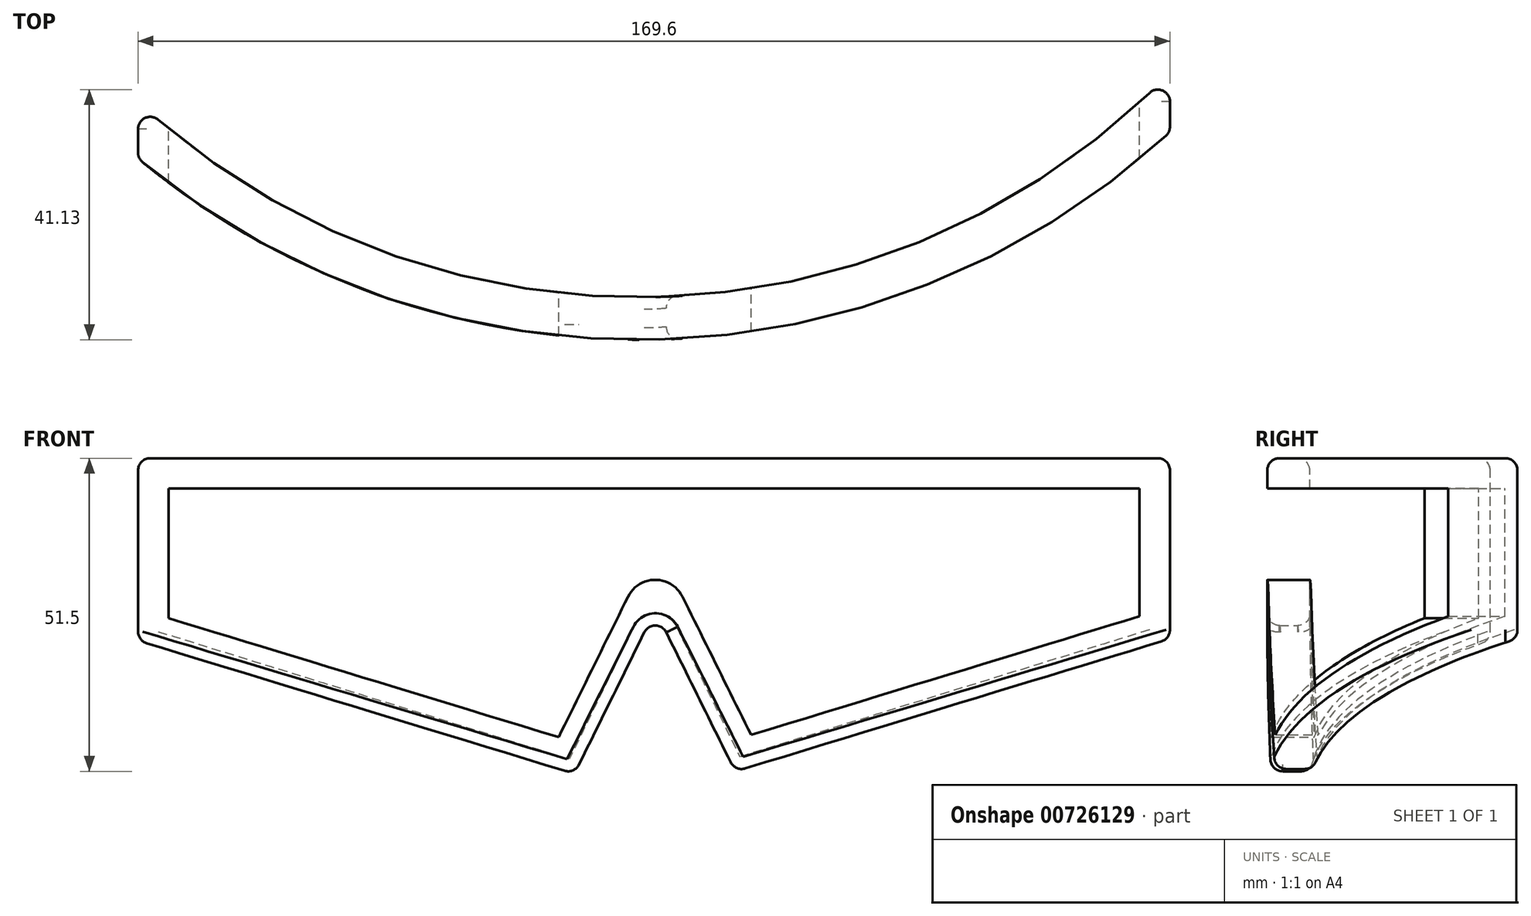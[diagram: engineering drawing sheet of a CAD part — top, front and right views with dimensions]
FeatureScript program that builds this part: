
annotation { "Feature Type Name" : "Feature", "Feature Type Description" : "" }
export const myFeature = defineFeature(function(context is Context, id is Id, definition is map)
    precondition{}
    {
        {
            var Q0;
            Q0=qCreatedBy(makeId("Front.planeOp"),FACE);
            var sketch = newSketch(context, id + "F0", { "sketchPlane" : qUnion([Q0])});
            skLineSegment(sketch, "E0.top", {"start": v(-14.32, 57.35) * mm, "end": v(-99.32, 57.35) * mm});
            skLineSegment(sketch, "E0.right", {"start": v(-99.32, 27.35) * mm, "end": v(-99.32, 57.35) * mm});
            skLineSegment(sketch, "E1", {"start": v(-27.59, 5.44) * mm, "end": v(-14.32, 32.35) * mm});
            skLineSegment(sketch, "E2", {"start": v(-27.59, 5.44) * mm, "end": v(-99.32, 27.35) * mm});
            skLineSegment(sketch, "E3.MirrorCS", {"start": v(-1.16, 5.82) * mm, "end": v(70.28, 27.64) * mm});
            skLineSegment(sketch, "E4.MirrorCS", {"start": v(70.28, 27.64) * mm, "end": v(70.28, 57.35) * mm});
            skLineSegment(sketch, "E5.MirrorCS", {"start": v(-14.32, 57.35) * mm, "end": v(70.28, 57.35) * mm});
            skLineSegment(sketch, "E6.MirrorCS", {"start": v(-1.16, 5.82) * mm, "end": v(-14.32, 32.35) * mm});
            skSolve(sketch);
        }
        {
            var Q0;
            Q0 = qSketchRegion(id + "F0", true);
            extrude(context, id + "F1", {"entities" : qUnion([Q0]), "depth" : 150 * mm, "offsetDistance" : 25 * mm});
        }
        {
            var Q0;
            Q0=qCreatedBy(makeId("Front.planeOp"),FACE);
            var sketch = newSketch(context, id + "F2", { "sketchPlane" : qUnion([Q0])});
            skLineSegment(sketch, "E7.0", {"start": v(65.28, 31.34) * mm, "end": v(1.43, 11.84) * mm});
            skLineSegment(sketch, "E7.1", {"start": v(65.28, 52.35) * mm, "end": v(65.28, 31.34) * mm});
            skLineSegment(sketch, "E7.2", {"start": v(-14.33, 43.62) * mm, "end": v(-30.2, 11.46) * mm});
            skLineSegment(sketch, "E7.3", {"start": v(-30.2, 11.46) * mm, "end": v(-94.32, 31.05) * mm});
            skLineSegment(sketch, "E7.4", {"start": v(-94.32, 31.05) * mm, "end": v(-94.32, 52.35) * mm});
            skLineSegment(sketch, "E7.5", {"start": v(1.43, 11.84) * mm, "end": v(-14.33, 43.62) * mm});
            skLineSegment(sketch, "E7.6", {"start": v(-94.32, 52.35) * mm, "end": v(65.28, 52.35) * mm});
            skSolve(sketch);
        }
        {
            var Q0;
            Q0 = qSketchRegion(id + "F2", true);
            extrude(context, id + "F3", {"entities" : qUnion([Q0]), "operationType" : NewBodyOperationType.REMOVE, "depth" : 200 * mm, "offsetDistance" : 25 * mm});
        }
        {
            var Q0;
            Q0=makeQuery(id+"F1.opExtrude","SWEPT_FACE",FACE,{"disambiguationData":[OSD([sQuery(id+"F0.wireOp",EDGE,"E0.top"),sQuery(id+"F0.wireOp",EDGE,"E5.MirrorCS")])]});
            var sketch = newSketch(context, id + "F4", { "sketchPlane" : qUnion([Q0])});
            skArc(sketch, "E8", {"start": v(-139.84, -48.26) * mm, "mid": v(-17.33, -138.81) * mm, "end": v(105.65, -48.9) * mm});
            skArc(sketch, "E9.0", {"start": v(-133.16, -46.2) * mm, "mid": v(-17.31, -131.81) * mm, "end": v(98.98, -46.8) * mm});
            skLineSegment(sketch, "E10", {"start": v(-139.84, -48.26) * mm, "end": v(-133.16, -46.2) * mm});
            skLineSegment(sketch, "E11", {"start": v(98.98, -46.8) * mm, "end": v(105.65, -48.9) * mm});
            skSolve(sketch);
        }
        {
            var Q0;
            Q0 = qSketchRegion(id + "F4", true);
            extrude(context, id + "F5", {"entities" : qUnion([Q0]), "operationType" : NewBodyOperationType.INTERSECT, "oppositeDirection" : true, "depth" : 150 * mm, "offsetDistance" : 25 * mm});
        }
        {
            var Q0;
            Q0=makeQuery(id+"F1.opExtrude","SWEPT_FACE",FACE,{"disambiguationData":[OSD([sQuery(id+"F0.wireOp",EDGE,"E0.right")])]});
            var Q1;
            Q1=makeQuery(id+"F1.opExtrude","SWEPT_FACE",FACE,{"disambiguationData":[OSD([sQuery(id+"F0.wireOp",EDGE,"E0.top"),sQuery(id+"F0.wireOp",EDGE,"E5.MirrorCS")])]});
            var Q2;
            Q2=makeQuery(id+"F1.opExtrude","SWEPT_FACE",FACE,{"disambiguationData":[OSD([sQuery(id+"F0.wireOp",EDGE,"E2")])]});
            var Q3;
            Q3=makeQuery(id+"F1.opExtrude","SWEPT_FACE",FACE,{"disambiguationData":[OSD([sQuery(id+"F0.wireOp",EDGE,"E6.MirrorCS")])]});
            var Q4;
            Q4=makeQuery(id+"F1.opExtrude","SWEPT_FACE",FACE,{"disambiguationData":[OSD([sQuery(id+"F0.wireOp",EDGE,"E1")])]});
            var Q5;
            Q5=makeQuery(id+"F1.opExtrude","SWEPT_FACE",FACE,{"disambiguationData":[OSD([sQuery(id+"F0.wireOp",EDGE,"E3.MirrorCS")])]});
            var Q6;
            Q6=makeQuery(id+"F1.opExtrude","SWEPT_FACE",FACE,{"disambiguationData":[OSD([sQuery(id+"F0.wireOp",EDGE,"E4.MirrorCS")])]});
            fillet(context, id + "F6", {"entities" : qUnion([Q0, Q1, Q2, Q3, Q4, Q5, Q6]), "radius" : 2 * mm, "tangentPropagation" : true, "allowEdgeOverflow" : false});
        }
        {
            var Q0;
            Q0=makeQuery(id+"F3.boolean.opBoolean","COPY",EDGE,{"derivedFrom":makeQuery(id+"F3.opExtrude","SWEPT_EDGE",EDGE,{"disambiguationData":[OSD([sQuery(id+"F2.wireOp",EDGE,"E7.2"),sQuery(id+"F2.wireOp",EDGE,"E7.5")])]})});
            fillet(context, id + "F7", {"entities" : qUnion([Q0]), "radius" : 5 * mm, "tangentPropagation" : true, "allowEdgeOverflow" : false});
        }
    });
